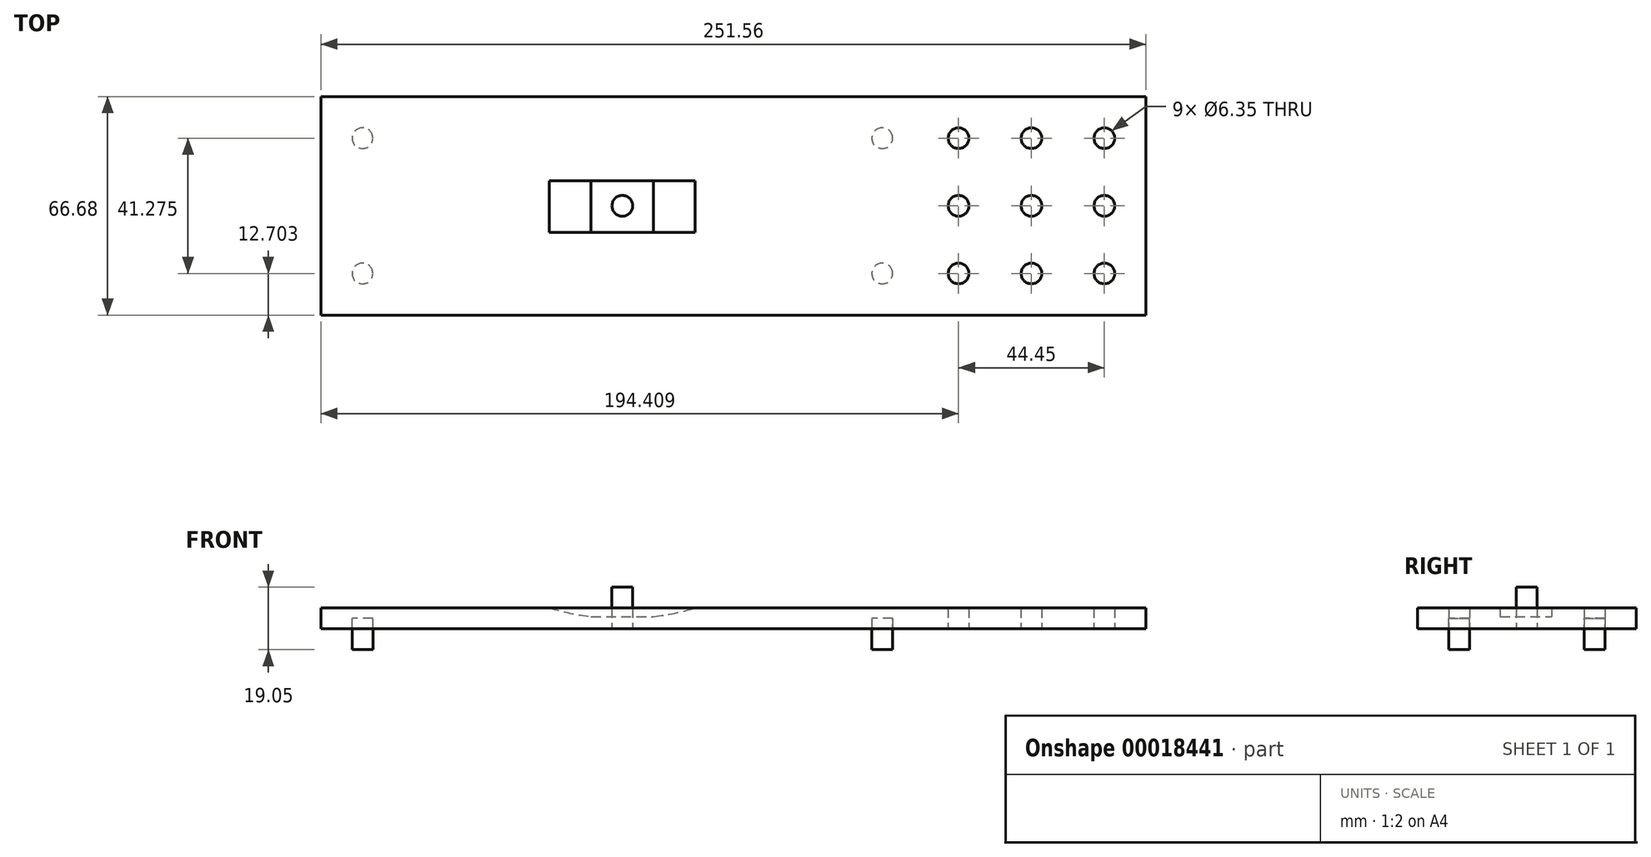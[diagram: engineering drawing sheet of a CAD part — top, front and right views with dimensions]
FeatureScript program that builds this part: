
annotation { "Feature Type Name" : "Feature", "Feature Type Description" : "" }
export const myFeature = defineFeature(function(context is Context, id is Id, definition is map)
    precondition{}
    {
        {
            var Q0;
            Q0=qCreatedBy(makeId("Top.planeOp"),FACE);
            var sketch = newSketch(context, id + "F0", { "sketchPlane" : qUnion([Q0])});
            skLineSegment(sketch, "E0.bottom", {"start": v(-66.52, 7.94) * mm, "end": v(66.52, 7.94) * mm});
            skLineSegment(sketch, "E0.top", {"start": v(-66.52, -7.94) * mm, "end": v(66.52, -7.94) * mm});
            skLineSegment(sketch, "E0.left", {"start": v(-66.52, 7.94) * mm, "end": v(-66.52, -7.94) * mm});
            skLineSegment(sketch, "E0.right", {"start": v(66.52, 7.94) * mm, "end": v(66.52, -7.94) * mm});
            skSolve(sketch);
        }
        {
            var Q0;
            Q0=qCreatedBy(makeId("Top.planeOp"),FACE);
            var sketch = newSketch(context, id + "F1", { "sketchPlane" : qUnion([Q0])});
            skLineSegment(sketch, "E1.0", {"start": v(159.64, 33.34) * mm, "end": v(-91.92, 33.34) * mm});
            skLineSegment(sketch, "E1.1", {"start": v(159.64, -33.34) * mm, "end": v(159.64, 33.34) * mm});
            skLineSegment(sketch, "E1.2", {"start": v(-91.92, -33.34) * mm, "end": v(159.64, -33.34) * mm});
            skLineSegment(sketch, "E1.3", {"start": v(-91.92, 33.34) * mm, "end": v(-91.92, -33.34) * mm});
            skSolve(sketch);
        }
        {
            var Q0;
            Q0=makeQuery(id+"F1.imprint","IMPRINT",FACE,{"disambiguationData":[TD([[makeQuery(id+"F1.imprint","IMPRINT",EDGE,{"derivedFrom":sQuery(id+"F1.wireOp",EDGE,"E1.0")}),1.0]])]});
            extrude(context, id + "F2", {"entities" : qUnion([Q0]), "depth" : 6.35 * mm});
        }
        {
            var Q0;
            Q0=makeQuery(id+"F2.opExtrude","CAP_FACE",FACE,{"disambiguationData":[OSD([sQuery(id+"F1.wireOp",EDGE,"E1.0"),sQuery(id+"F1.wireOp",EDGE,"E1.1"),sQuery(id+"F1.wireOp",EDGE,"E1.2"),sQuery(id+"F1.wireOp",EDGE,"E1.3")])],"isStart":false});
            var sketch = newSketch(context, id + "F3", { "sketchPlane" : qUnion([Q0])});
            skLineSegment(sketch, "E2.bottom", {"start": v(-22.22, 6.35) * mm, "end": v(22.23, 6.35) * mm});
            skLineSegment(sketch, "E2.top", {"start": v(-22.22, -6.35) * mm, "end": v(22.23, -6.35) * mm});
            skLineSegment(sketch, "E2.left", {"start": v(-22.22, 6.35) * mm, "end": v(-22.22, -6.35) * mm});
            skLineSegment(sketch, "E2.right", {"start": v(22.23, 6.35) * mm, "end": v(22.23, -6.35) * mm});
            skSolve(sketch);
        }
        {
            var Q0;
            Q0=qCreatedBy(makeId("Front.planeOp"),FACE);
            var sketch = newSketch(context, id + "F4", { "sketchPlane" : qUnion([Q0])});
            skLineSegment(sketch, "E3.0", {"start": v(-22.22, 6.35) * mm, "end": v(22.23, 6.35) * mm});
            skArc(sketch, "E4", {"start": v(-22.22, 6.35) * mm, "mid": v(-15.93, 4.76) * mm, "end": v(-9.52, 3.7) * mm});
            skArc(sketch, "E5.trimOffspring", {"start": v(9.53, 3.7) * mm, "mid": v(15.93, 4.76) * mm, "end": v(22.22, 6.35) * mm});
            skLineSegment(sketch, "E6", {"start": v(-9.52, 3.7) * mm, "end": v(9.53, 3.7) * mm});
            skSolve(sketch);
        }
        {
            var Q0;
            Q0 = qSketchRegion(id + "F4", true);
            extrude(context, id + "F5", {"entities" : qUnion([Q0]), "operationType" : NewBodyOperationType.REMOVE, "depth" : 8.14 * mm, "hasSecondDirection" : true, "secondDirectionOppositeDirection" : true, "secondDirectionDepth" : 7.63 * mm});
        }
        {
            var Q0;
            Q0=qCreatedBy(makeId("Top.planeOp"),FACE);
            var sketch = newSketch(context, id + "F6", { "sketchPlane" : qUnion([Q0])});
            skCircle(sketch, "E7", {"center": v(0, 0) * mm, "radius": 3.18 * mm});
            skSolve(sketch);
        }
        {
            var Q0;
            Q0 = qSketchRegion(id + "F6", true);
            extrude(context, id + "F7", {"entities" : qUnion([Q0]), "depth" : 12.7 * mm});
        }
        {
            var Q0;
            Q0=qCreatedBy(makeId("Top.planeOp"),FACE);
            var sketch = newSketch(context, id + "F8", { "sketchPlane" : qUnion([Q0])});
            skCircle(sketch, "E8", {"center": v(-79.22, 20.64) * mm, "radius": 3.18 * mm});
            skCircle(sketch, "E9.MirrorC", {"center": v(79.22, 20.64) * mm, "radius": 3.18 * mm});
            skCircle(sketch, "E10.MirrorC", {"center": v(79.22, -20.64) * mm, "radius": 3.18 * mm});
            skCircle(sketch, "E11.MirrorC", {"center": v(-79.22, -20.64) * mm, "radius": 3.18 * mm});
            skSolve(sketch);
        }
        {
            var Q0;
            Q0 = qSketchRegion(id + "F8", true);
            extrude(context, id + "F9", {"entities" : qUnion([Q0]), "oppositeDirection" : true, "depth" : 6.35 * mm, "hasSecondDirection" : true, "secondDirectionOppositeDirection" : false, "secondDirectionDepth" : 3.17 * mm});
        }
        {
            var Q0;
            Q0=qCreatedBy(makeId("Top.planeOp"),FACE);
            var sketch = newSketch(context, id + "F10", { "sketchPlane" : qUnion([Q0])});
            skCircle(sketch, "E12", {"center": v(102.49, 20.64) * mm, "radius": 3.18 * mm});
            skCircle(sketch, "E13.0.1.0", {"center": v(102.49, 0) * mm, "radius": 3.18 * mm});
            skCircle(sketch, "E13.0.2.0", {"center": v(102.49, -20.64) * mm, "radius": 3.18 * mm});
            skCircle(sketch, "E13.1.0.0", {"center": v(124.71, 20.64) * mm, "radius": 3.18 * mm});
            skCircle(sketch, "E13.1.1.0", {"center": v(124.71, 0) * mm, "radius": 3.18 * mm});
            skCircle(sketch, "E13.1.2.0", {"center": v(124.71, -20.64) * mm, "radius": 3.18 * mm});
            skCircle(sketch, "E13.2.0.0", {"center": v(146.94, 20.64) * mm, "radius": 3.18 * mm});
            skCircle(sketch, "E13.2.1.0", {"center": v(146.94, 0) * mm, "radius": 3.18 * mm});
            skCircle(sketch, "E13.2.2.0", {"center": v(146.94, -20.64) * mm, "radius": 3.18 * mm});
            skLineSegment(sketch, "E13.direction1", {"start": v(102.49, 20.64) * mm, "end": v(124.71, 20.64) * mm, "construction": true});
            skLineSegment(sketch, "E13.direction2", {"start": v(102.49, 20.64) * mm, "end": v(102.49, 0) * mm, "construction": true});
            skSolve(sketch);
        }
        {
            var Q0;
            Q0 = qSketchRegion(id + "F10", true);
            extrude(context, id + "F11", {"entities" : qUnion([Q0]), "operationType" : NewBodyOperationType.REMOVE, "depth" : 6.35 * mm});
        }
        {
            var Q0;
            Q0 = qSketchRegion(id + "F8", true);
            extrude(context, id + "F12", {"entities" : qUnion([Q0]), "depth" : 3.17 * mm});
        }
    });
